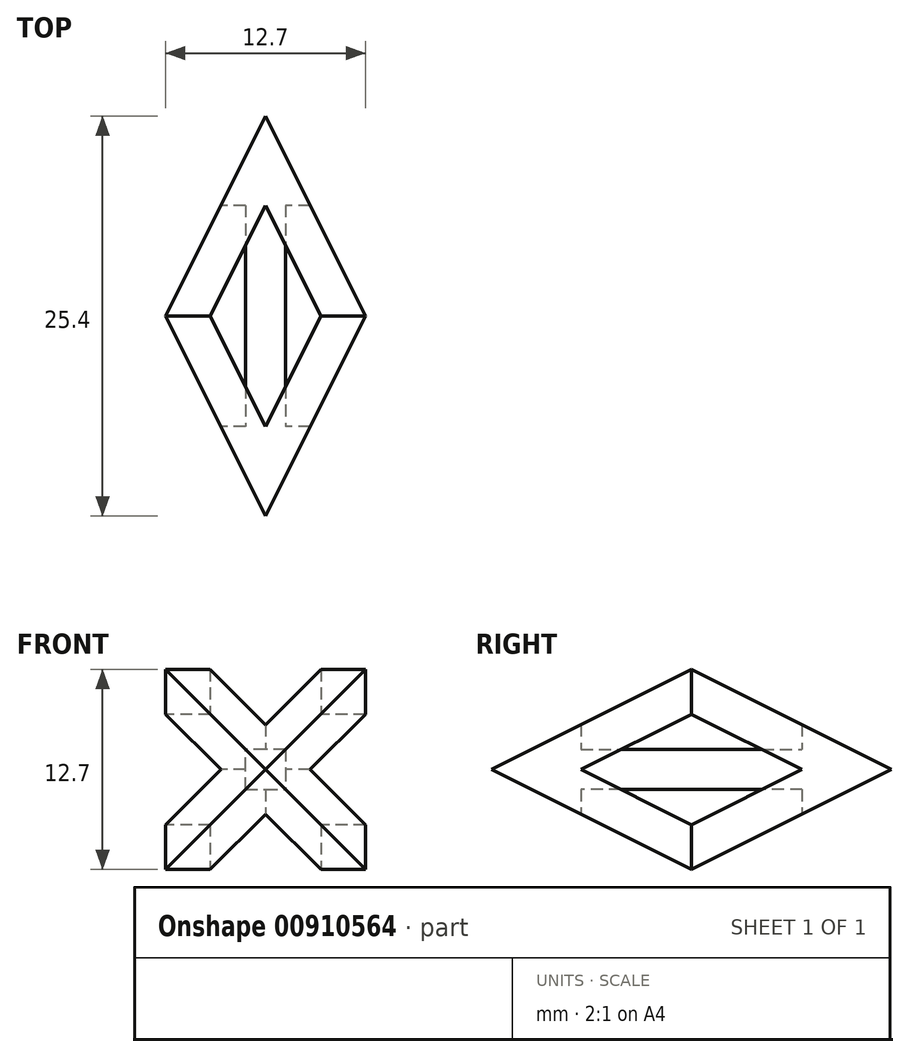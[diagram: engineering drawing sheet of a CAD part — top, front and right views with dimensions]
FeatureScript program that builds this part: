
annotation { "Feature Type Name" : "Feature", "Feature Type Description" : "" }
export const myFeature = defineFeature(function(context is Context, id is Id, definition is map)
    precondition{}
    {
        {
            var Q0;
            Q0=qCreatedBy(makeId("Right.planeOp"),FACE);
            var sketch = newSketch(context, id + "F0", { "sketchPlane" : qUnion([Q0])});
            skLineSegment(sketch, "E0.bottom", {"start": v(12.7, 6.35) * mm, "end": v(-12.7, 6.35) * mm});
            skLineSegment(sketch, "E0.top", {"start": v(12.7, -6.35) * mm, "end": v(-12.7, -6.35) * mm});
            skLineSegment(sketch, "E0.left", {"start": v(12.7, 6.35) * mm, "end": v(12.7, -6.35) * mm});
            skLineSegment(sketch, "E0.right", {"start": v(-12.7, 6.35) * mm, "end": v(-12.7, -6.35) * mm});
            skPoint(sketch, "E0.middle", {"position": v(0, 0) * mm});
            skSolve(sketch);
        }
        {
            var Q0;
            Q0=makeQuery(id+"F0.imprint","IMPRINT",FACE,{"disambiguationData":[TD([[makeQuery(id+"F0.imprint","IMPRINT",EDGE,{"derivedFrom":sQuery(id+"F0.wireOp",EDGE,"E0.bottom")}),1.0]])]});
            extrude(context, id + "F1", {"entities" : qUnion([Q0]), "depth" : 12.7 * mm, "offsetDistance" : 25.4 * mm});
        }
        {
            var Q0;
            Q0=makeQuery(id+"F1.opExtrude","SWEPT_FACE",FACE,{"disambiguationData":[OSD([sQuery(id+"F0.wireOp",EDGE,"E0.top")])]});
            var sketch = newSketch(context, id + "F2", { "sketchPlane" : qUnion([Q0])});
            skLineSegment(sketch, "E1", {"start": v(0, 0) * mm, "end": v(6.35, -12.7) * mm});
            skLineSegment(sketch, "E2", {"start": v(6.35, -12.7) * mm, "end": v(12.7, 0) * mm});
            skLineSegment(sketch, "E3", {"start": v(12.7, 0) * mm, "end": v(6.35, 12.7) * mm});
            skLineSegment(sketch, "E4", {"start": v(6.35, 12.7) * mm, "end": v(0, 0) * mm});
            skLineSegment(sketch, "E5", {"start": v(2.84, 0) * mm, "end": v(6.35, 7.02) * mm});
            skLineSegment(sketch, "E6", {"start": v(6.35, 7.02) * mm, "end": v(9.86, 0) * mm});
            skLineSegment(sketch, "E7", {"start": v(9.86, 0) * mm, "end": v(6.35, -7.02) * mm});
            skLineSegment(sketch, "E8", {"start": v(6.35, -7.02) * mm, "end": v(2.84, 0) * mm});
            skSolve(sketch);
        }
        {
            var Q0;
            Q0=makeQuery(id+"F1.opExtrude","CAP_FACE",FACE,{"disambiguationData":[OSD([sQuery(id+"F0.wireOp",EDGE,"E0.bottom"),sQuery(id+"F0.wireOp",EDGE,"E0.top"),sQuery(id+"F0.wireOp",EDGE,"E0.left"),sQuery(id+"F0.wireOp",EDGE,"E0.right")])],"isStart":true});
            var sketch = newSketch(context, id + "F3", { "sketchPlane" : qUnion([Q0])});
            skLineSegment(sketch, "E9", {"start": v(12.7, 0) * mm, "end": v(0, 6.35) * mm});
            skLineSegment(sketch, "E10", {"start": v(0, 6.35) * mm, "end": v(-12.7, 0) * mm});
            skLineSegment(sketch, "E11", {"start": v(-12.7, 0) * mm, "end": v(0, -6.35) * mm});
            skLineSegment(sketch, "E12", {"start": v(0, -6.35) * mm, "end": v(12.7, 0) * mm});
            skLineSegment(sketch, "E13", {"start": v(0, 3.51) * mm, "end": v(7.02, 0) * mm});
            skLineSegment(sketch, "E14", {"start": v(7.02, 0) * mm, "end": v(0, -3.51) * mm});
            skLineSegment(sketch, "E15", {"start": v(0, -3.51) * mm, "end": v(-7.02, 0) * mm});
            skLineSegment(sketch, "E16", {"start": v(-7.02, 0) * mm, "end": v(0, 3.51) * mm});
            skSolve(sketch);
        }
        {
            var Q0;
            Q0=makeQuery(id+"F1.opExtrude","SWEPT_FACE",FACE,{"disambiguationData":[OSD([sQuery(id+"F0.wireOp",EDGE,"E0.left")])]});
            var sketch = newSketch(context, id + "F4", { "sketchPlane" : qUnion([Q0])});
            skLineSegment(sketch, "E17.bottom", {"start": v(-7.62, 1.27) * mm, "end": v(-5.08, 1.27) * mm});
            skLineSegment(sketch, "E17.top", {"start": v(-7.62, -1.27) * mm, "end": v(-5.08, -1.27) * mm});
            skLineSegment(sketch, "E17.left", {"start": v(-7.62, 1.27) * mm, "end": v(-7.62, -1.27) * mm});
            skLineSegment(sketch, "E17.right", {"start": v(-5.08, 1.27) * mm, "end": v(-5.08, -1.27) * mm});
            skPoint(sketch, "E17.middle", {"position": v(-6.35, 0) * mm});
            skSolve(sketch);
        }
        {
            var Q0;
            Q0=makeQuery(id+"F3.imprint","IMPRINT",FACE,{"disambiguationData":[TD([[makeQuery(id+"F3.imprint","IMPRINT",EDGE,{"derivedFrom":sQuery(id+"F3.wireOp",EDGE,"E13")}),-1.0]])]});
            extrude(context, id + "F5", {"entities" : qUnion([Q0]), "operationType" : NewBodyOperationType.REMOVE, "oppositeDirection" : true, "depth" : 12.7 * mm, "offsetDistance" : 25.4 * mm});
        }
        {
            var Q0;
            Q0=makeQuery(id+"F2.imprint","IMPRINT",FACE,{"disambiguationData":[TD([[makeQuery(id+"F2.imprint","IMPRINT",EDGE,{"derivedFrom":sQuery(id+"F2.wireOp",EDGE,"E5")}),-1.0]])]});
            extrude(context, id + "F6", {"entities" : qUnion([Q0]), "operationType" : NewBodyOperationType.REMOVE, "oppositeDirection" : true, "depth" : 12.7 * mm, "offsetDistance" : 25.4 * mm});
        }
        {
            var Q0;
            Q0=makeQuery(id+"F4.imprint","IMPRINT",FACE,{"disambiguationData":[TD([[makeQuery(id+"F4.imprint","IMPRINT",EDGE,{"derivedFrom":sQuery(id+"F4.wireOp",EDGE,"E17.bottom")}),-1.0]])]});
            extrude(context, id + "F7", {"entities" : qUnion([Q0]), "operationType" : NewBodyOperationType.ADD, "depth" : 0 * mm, "offsetDistance" : 25.4 * mm, "hasSecondDirection" : true, "secondDirectionOppositeDirection" : true, "secondDirectionDepth" : 25.4 * mm});
        }
        {
            var Q0;
            {var subQ0=sQuery(id+"F2.wireOp",EDGE,"E1");Q0=makeQuery(id+"F2.imprint","IMPRINT",FACE,{"disambiguationData":[TD([[makeQuery(id+"F2.imprint","IMPRINT",EDGE,{"derivedFrom":subQ0}),-1.0]])]});}
            var Q1;
            {var subQ0=sQuery(id+"F2.wireOp",EDGE,"E2");Q1=makeQuery(id+"F2.imprint","IMPRINT",FACE,{"disambiguationData":[TD([[makeQuery(id+"F2.imprint","IMPRINT",EDGE,{"derivedFrom":subQ0}),-1.0]])]});}
            var Q2;
            {var subQ0=sQuery(id+"F2.wireOp",EDGE,"E3");Q2=makeQuery(id+"F2.imprint","IMPRINT",FACE,{"disambiguationData":[TD([[makeQuery(id+"F2.imprint","IMPRINT",EDGE,{"derivedFrom":subQ0}),-1.0]])]});}
            var Q3;
            {var subQ0=sQuery(id+"F2.wireOp",EDGE,"E4");Q3=makeQuery(id+"F2.imprint","IMPRINT",FACE,{"disambiguationData":[TD([[makeQuery(id+"F2.imprint","IMPRINT",EDGE,{"derivedFrom":subQ0}),-1.0]])]});}
            extrude(context, id + "F8", {"entities" : qUnion([Q0, Q1, Q2, Q3]), "operationType" : NewBodyOperationType.REMOVE, "oppositeDirection" : true, "depth" : 12.7 * mm, "offsetDistance" : 25.4 * mm});
        }
        {
            var Q0;
            {var subQ0=sQuery(id+"F3.wireOp",EDGE,"E11");Q0=makeQuery(id+"F3.imprint","IMPRINT",FACE,{"disambiguationData":[TD([[makeQuery(id+"F3.imprint","IMPRINT",EDGE,{"derivedFrom":subQ0}),-1.0]])]});}
            var Q1;
            {var subQ0=sQuery(id+"F3.wireOp",EDGE,"E10");Q1=makeQuery(id+"F3.imprint","IMPRINT",FACE,{"disambiguationData":[TD([[makeQuery(id+"F3.imprint","IMPRINT",EDGE,{"derivedFrom":subQ0}),-1.0]])]});}
            var Q2;
            {var subQ0=sQuery(id+"F3.wireOp",EDGE,"E9");Q2=makeQuery(id+"F3.imprint","IMPRINT",FACE,{"disambiguationData":[TD([[makeQuery(id+"F3.imprint","IMPRINT",EDGE,{"derivedFrom":subQ0}),-1.0]])]});}
            var Q3;
            {var subQ0=sQuery(id+"F3.wireOp",EDGE,"E12");Q3=makeQuery(id+"F3.imprint","IMPRINT",FACE,{"disambiguationData":[TD([[makeQuery(id+"F3.imprint","IMPRINT",EDGE,{"derivedFrom":subQ0}),-1.0]])]});}
            extrude(context, id + "F9", {"entities" : qUnion([Q0, Q1, Q2, Q3]), "operationType" : NewBodyOperationType.REMOVE, "oppositeDirection" : true, "depth" : 12.7 * mm, "offsetDistance" : 25.4 * mm});
        }
    });
